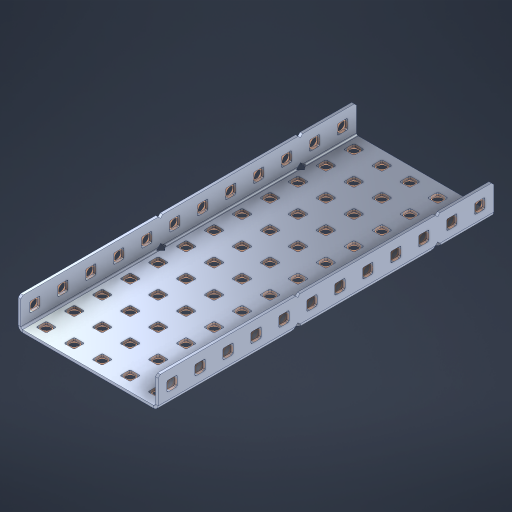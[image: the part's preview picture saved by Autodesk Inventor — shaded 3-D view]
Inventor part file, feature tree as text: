
AUTODESK INVENTOR PART (.ipt)
format: ipt  version: 2023 (Build 270158000, 158)  size: 1,167,360 bytes
history: native  units: in
note: dims shown in document units (in); Inventor stores cm internally (conversion verified against a paired STEP export)
features: other x89, extrude x83, sheet_metal_op x10, sketch x8, mirror x1, pattern_linear x1, chamfer x1
ambient origin geometry x8: Origin, YZ Plane, XZ Plane, XY Plane, X Axis, Y Axis, Z Axis, Center Point
bodies: Solid1 (feature_tree), Body (feature_tree)
feature tree (193):
  other  "Flange Pattern Plane"
  sheet_metal_op  "Flange Pattern"
  sheet_metal_op  "Body Pattern"
  other  "Arc Length"
  mirror  "Notch Mirror"
  pattern_linear  "Notch Pattern"  Spacing1=0.1875in  [1 undecoded]
  chamfer  "End Chamfer"
  extrude  "Half Cut"  Depth=0.0469in
  sketch  "Sketch1"  dims[d0=2.5in]
  other  "Plate1"
  sketch  "Sketch2"  dims[d1=6.0in]
  other  "Plate2"
  sheet_metal_op  "Bend1"
  sheet_metal_op  "Corner1"
  sketch  "Sketch3"  dims[d2=0.0469in]
  other  "Flange Pattern Sketch"
  sketch  "Sketch7"  dims[d3=0.0469in]
  other  "Srf1"
  other  "Srf2"
  sketch  "Sketch8"  dims[d4=0.0234in]
  sketch  "Sketch9"  dims[d5=0.0938in]
  other  "Srf91"
  sheet_metal_op  "Body Pattern Sketch"
  other  "Srf92"
  sketch  "Sketch13"  dims[d6=0.0469in]
  sketch  "Sketch14"  dims[d7=0.5in d8=90.0deg d9=0.0312in d10=0.1875in d11=0.0469in d12=0.0469in d16=0.182in d17=0.02in d18=0.0469in d19=0.0in d20=0.25in d21=0.25in d46=0.172in d47=1.0in d48=0.0in d49=0.182in d50=0.02in d51=0.25in d52=0.25in d53=0.0469in d54=0.0in d55=0.172in d56=1.0in d57=0.0in d60=4.7244in d62=0.5in d63=1.9685in d65=0.5in d85=0.1227in d86=0.1659in d88=0.04in d89=0.0469in d90=0.0in d91=0.04in d92=0.0491in d95=2.5in d96=0.04in d97=0.25in d98=45.0deg d101=0.0in d102=2.497in d131=2.5in d132=4.7244in d134=0.5in d139=0.5in]
  other  "Srf856"
  other  "Srf1310"
  other  "Srf1311"
  other  "Srf1312"
  other  "Srf1376"
  other  "Srf1377"
  other  "Srf1728"
  other  "Srf1755"
  other  "Srf1878"
  other  "Srf1879"
  other  "Srf1880"
  other  "Srf1881"
  other  "Srf1882"
  other  "Srf1883"
  other  "Srf1884"
  other  "Srf1885"
  other  "Srf1886"
  other  "Srf1887"
  other  "Srf1888"
  other  "Srf1889"
  other  "Srf1890"
  other  "Srf1891"
  other  "Srf1892"
  other  "Srf1893"
  other  "Srf1894"
  other  "Srf1895"
  other  "Srf1942"
  other  "Srf1943"
  other  "Srf1944"
  other  "Srf1945"
  other  "Srf1946"
  other  "Srf1947"
  other  "Srf1948"
  other  "Srf1949"
  other  "Srf1950"
  other  "Srf1951"
  other  "Srf1952"
  other  "Srf1953"
  other  "Srf1954"
  other  "Srf1955"
  other  "Srf1956"
  other  "Srf1957"
  other  "Srf1958"
  other  "Srf1959"
  other  "Srf1960"
  other  "Srf1961"
  other  "Srf1962"
  other  "Srf1963"
  other  "Srf1964"
  other  "Srf1965"
  other  "Srf1966"
  other  "Srf1967"
  other  "Srf1968"
  other  "Srf1969"
  other  "Srf1970"
  other  "Srf2146"
  other  "Srf2147"
  other  "Srf2148"
  other  "Srf2149"
  other  "Srf2150"
  other  "Srf2151"
  other  "Srf2152"
  other  "Srf2153"
  other  "Srf2154"
  other  "Srf2155"
  other  "Srf2156"
  other  "Srf2157"
  other  "Srf2158"
  other  "Srf2159"
  other  "Srf2160"
  other  "Srf2161"
  other  "Srf2162"
  other  "Srf2163"
  other  "Srf2164"
  other  "Srf2165"
  other  "Srf2166"
  other  "Srf2167"
  other  "Srf2168"
  other  "Srf2169"
  other  "Srf2170"
  sheet_metal_op  "Flange Stamp"
  sheet_metal_op  "Flange Circle"
  sheet_metal_op  "Body Stamp"
  sheet_metal_op  "Body Circle"
  sheet_metal_op  "Notch"
  extrude  "ExtrusionSrf2"  Depth=0.0469in
  extrude  "ExtrusionSrf92"  Depth=2.5in
  extrude  "ExtrusionSrf856"  Depth=0.02in
  extrude  "ExtrusionSrf1310"  Depth=0.0469in
  extrude  "ExtrusionSrf1311"  TaperAngle=0.0deg  [1 undecoded]
  extrude  "ExtrusionSrf1312"  Depth=0.25in
  extrude  "ExtrusionSrf1376"  Depth=0.25in
  extrude  "ExtrusionSrf1377"  Depth=2.5in
  extrude  "ExtrusionSrf1728"  Depth=2.5in TaperAngle=0.0deg
  extrude  "ExtrusionSrf1755"  Depth=2.5in
  extrude  "ExtrusionSrf1878"  Depth=0.02in
  extrude  "ExtrusionSrf1879"  Depth=0.25in
  extrude  "ExtrusionSrf1880"  Depth=0.25in
  extrude  "ExtrusionSrf1881"  Depth=0.0469in
  extrude  "ExtrusionSrf1882"  TaperAngle=0.0deg  [1 undecoded]
  extrude  "ExtrusionSrf1883"  Depth=2.5in
  extrude  "ExtrusionSrf1884"  Depth=2.5in TaperAngle=0.0deg
  extrude  "ExtrusionSrf1885"  Depth=2.5in
  extrude  "ExtrusionSrf1886"  Depth=2.5in
  extrude  "ExtrusionSrf1887"  Depth=2.5in
  extrude  "ExtrusionSrf1888"  Depth=2.5in
  extrude  "ExtrusionSrf1889"  Depth=2.5in
  extrude  "ExtrusionSrf1890"  Depth=0.0469in
  extrude  "ExtrusionSrf1891"  TaperAngle=0.0deg  [1 undecoded]
  extrude  "ExtrusionSrf1892"  Depth=2.5in
  extrude  "ExtrusionSrf1893"  Depth=2.5in
  extrude  "ExtrusionSrf1894"  Depth=2.5in
  extrude  "ExtrusionSrf1895"  Depth=0.25in TaperAngle=45.0deg
  extrude  "ExtrusionSrf1942"  TaperAngle=0.0deg  [1 undecoded]
  extrude  "ExtrusionSrf1943"  Depth=2.5in
  extrude  "ExtrusionSrf1944"  Depth=2.5in
  extrude  "ExtrusionSrf1945"  Depth=2.5in
  extrude  "ExtrusionSrf1946"  Depth=2.5in
  extrude  "ExtrusionSrf1947"  Depth=2.5in
  extrude  "ExtrusionSrf1948"  [1 undecoded]
  extrude  "ExtrusionSrf1949"  [1 undecoded]
  extrude  "ExtrusionSrf1950"  [1 undecoded]
  extrude  "ExtrusionSrf1951"  [1 undecoded]
  extrude  "ExtrusionSrf1952"  [1 undecoded]
  extrude  "ExtrusionSrf1953"  [1 undecoded]
  extrude  "ExtrusionSrf1954"  [1 undecoded]
  extrude  "ExtrusionSrf1955"  [1 undecoded]
  extrude  "ExtrusionSrf1956"  [1 undecoded]
  extrude  "ExtrusionSrf1957"  [1 undecoded]
  extrude  "ExtrusionSrf1958"  [1 undecoded]
  extrude  "ExtrusionSrf1959"  [1 undecoded]
  extrude  "ExtrusionSrf1960"  [1 undecoded]
  extrude  "ExtrusionSrf1961"  [1 undecoded]
  extrude  "ExtrusionSrf1962"  [1 undecoded]
  extrude  "ExtrusionSrf1963"  [1 undecoded]
  extrude  "ExtrusionSrf1964"  [1 undecoded]
  extrude  "ExtrusionSrf1965"  [1 undecoded]
  extrude  "ExtrusionSrf1966"  [1 undecoded]
  extrude  "ExtrusionSrf1967"  [1 undecoded]
  extrude  "ExtrusionSrf1968"  [1 undecoded]
  extrude  "ExtrusionSrf1969"  [1 undecoded]
  extrude  "ExtrusionSrf1970"  [1 undecoded]
  extrude  "ExtrusionSrf2146"  [1 undecoded]
  extrude  "ExtrusionSrf2147"  [1 undecoded]
  extrude  "ExtrusionSrf2148"  [1 undecoded]
  extrude  "ExtrusionSrf2149"  [1 undecoded]
  extrude  "ExtrusionSrf2150"  [1 undecoded]
  extrude  "ExtrusionSrf2151"  [1 undecoded]
  extrude  "ExtrusionSrf2152"  [1 undecoded]
  extrude  "ExtrusionSrf2153"  [1 undecoded]
  extrude  "ExtrusionSrf2154"  [1 undecoded]
  extrude  "ExtrusionSrf2155"  [1 undecoded]
  extrude  "ExtrusionSrf2156"  [1 undecoded]
  extrude  "ExtrusionSrf2157"  [1 undecoded]
  extrude  "ExtrusionSrf2158"  [1 undecoded]
  extrude  "ExtrusionSrf2159"  [1 undecoded]
  extrude  "ExtrusionSrf2160"  [1 undecoded]
  extrude  "ExtrusionSrf2161"  [1 undecoded]
  extrude  "ExtrusionSrf2162"  [1 undecoded]
  extrude  "ExtrusionSrf2163"  [1 undecoded]
  extrude  "ExtrusionSrf2164"  [1 undecoded]
  extrude  "ExtrusionSrf2165"  [1 undecoded]
  extrude  "ExtrusionSrf2166"  [1 undecoded]
  extrude  "ExtrusionSrf2167"  [1 undecoded]
  extrude  "ExtrusionSrf2168"  [1 undecoded]
  extrude  "ExtrusionSrf2169"  [1 undecoded]
  extrude  "ExtrusionSrf2170"  [1 undecoded]
note: 53 required parameter values undecoded (feature->parameter linkage not recoverable at this tier; creation-order binding heuristic only, values carry confidence <= 0.55)
